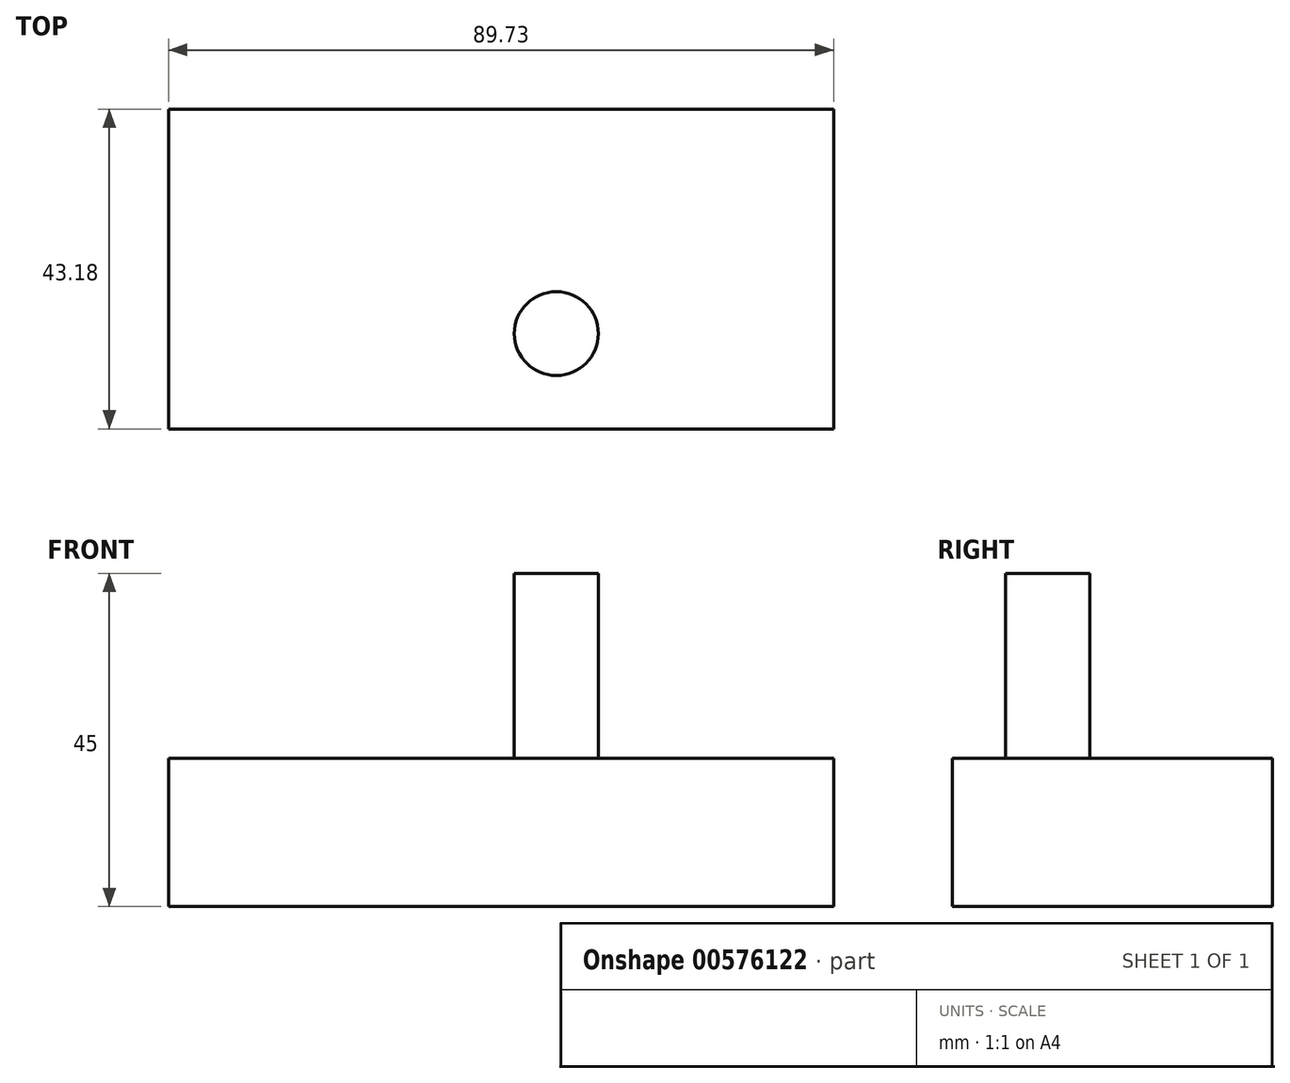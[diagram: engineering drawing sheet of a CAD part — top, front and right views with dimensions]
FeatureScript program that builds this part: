
annotation { "Feature Type Name" : "Feature", "Feature Type Description" : "" }
export const myFeature = defineFeature(function(context is Context, id is Id, definition is map)
    precondition{}
    {
        {
            var Q0;
            Q0=qCreatedBy(makeId("Top.planeOp"),FACE);
            var sketch = newSketch(context, id + "F0", { "sketchPlane" : qUnion([Q0])});
            skLineSegment(sketch, "E0.bottom", {"start": v(-35.72, 30.31) * mm, "end": v(54, 30.31) * mm});
            skLineSegment(sketch, "E0.top", {"start": v(-35.72, -12.87) * mm, "end": v(54, -12.87) * mm});
            skLineSegment(sketch, "E0.left", {"start": v(-35.72, 30.31) * mm, "end": v(-35.72, -12.87) * mm});
            skLineSegment(sketch, "E0.right", {"start": v(54, 30.31) * mm, "end": v(54, -12.87) * mm});
            skSolve(sketch);
        }
        {
            var Q0;
            Q0=makeQuery(id+"F0.imprint","IMPRINT",FACE,{"disambiguationData":[TD([[makeQuery(id+"F0.imprint","IMPRINT",EDGE,{"derivedFrom":sQuery(id+"F0.wireOp",EDGE,"E0.bottom")}),-1.0]])]});
            extrude(context, id + "F1", {"entities" : qUnion([Q0]), "depth" : 20 * mm, "offsetDistance" : 25 * mm});
        }
        {
            var Q0;
            Q0=makeQuery(id+"F1.opExtrude","CAP_FACE",FACE,{"disambiguationData":[OSD([sQuery(id+"F0.wireOp",EDGE,"E0.bottom"),sQuery(id+"F0.wireOp",EDGE,"E0.top"),sQuery(id+"F0.wireOp",EDGE,"E0.left"),sQuery(id+"F0.wireOp",EDGE,"E0.right")])],"isStart":false});
            var sketch = newSketch(context, id + "F2", { "sketchPlane" : qUnion([Q0])});
            skCircle(sketch, "E1", {"center": v(16.6, 0) * mm, "radius": 5.66 * mm});
            skSolve(sketch);
        }
        {
            var Q0;
            Q0 = qSketchRegion(id + "F2", true);
            extrude(context, id + "F3", {"entities" : qUnion([Q0]), "operationType" : NewBodyOperationType.ADD, "depth" : 25 * mm, "offsetDistance" : 25 * mm});
        }
    });
